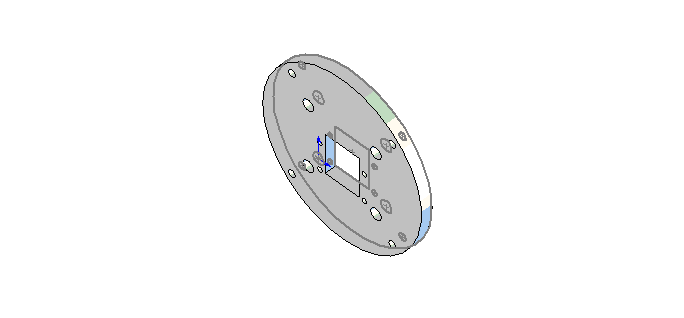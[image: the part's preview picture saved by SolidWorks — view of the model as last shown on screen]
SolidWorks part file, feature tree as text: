
SOLIDWORKS PART (.sldprt)
format: sldprt  version: not decoded by parser v0  size: 305,664 bytes
history: native  units: mm
features: sketch x4, plane x3, extrude x1 + 1 further entry (+7 scaffold rows collapsed)
feature tree (16):
  scaffold x7  (default folders/planes/origin — collapsed)
  "Corps de surface"
  plane  "Face"
  plane  "Dessus"
  plane  "Droite"
  sketch  "Esquisse1"  dims[c1.D1=4.8mm c1.D2=4.8mm c1.D7=4.8mm c1.D8=4.8mm c1.D17=~42.860884mm c1.D18=~42.860884mm c1.D3=32.0mm c1.D4=4.8mm c1.D5=8.0mm c1.D6=8.0mm c2.D7=4.8mm c2.D4=4.0mm c2.D5=5.6mm c2.D6=48.0mm c2.D9=32.0mm c2.D10=4.0mm c2.D11=5.6mm c2.D12=48.0mm c2.D13=28.8mm c2.D14=8.0mm c2.D15=8.0mm c2.D16=16.0mm c2.D18=48.0mm c3.D16=16.0mm c3.D17=8.0mm c3.D18=8.0mm c3.D19=4.0mm c3.D20=4.0mm c3.D21=24.0mm c3.D22=25.0mm c3.D13=28.8mm c3.D3=64.0mm c3.D12=8.0mm c4.D17=8.0mm c4.D9=8.0mm c4.D12=64.0mm c5.D17=48.0mm c5.D18=8.0mm c5.D9=32.0mm c6.D17=16.0mm c6.D18=16.0mm]
  sketch  "Esquisse5"  dims[c1.D12=2.1mm c1.D16=2.1mm c1.D1=8.0mm c1.D2=8.0mm c1.D3=4.0mm c1.D4=4.0mm c1.D5=25.0mm c1.D6=24.0mm c1.D7=12.5mm c1.D8=9.6mm c1.D9=5.5mm c1.D10=20.8mm c1.D11=10.4mm c1.D13=9.5mm c1.D14=2.0mm c1.D15=12.5mm c2.D16=~5.972653mm]
  sketch  "Esquisse7"  dims[c1.D1=75.0mm c1.D2=60.0mm c1.D3=3.1mm c1.D4=33.5mm c1.D5=33.5mm c2.D5=45.0deg c2.D6=~23.688077mm]
  sketch  "Esquisse6"  dims[D1=75.0mm D5=5.0mm D6=5.0mm D7=5.0mm D8=5.0mm D9=2.1mm D10=2.1mm D11=2.1mm D12=2.1mm D13=3.1mm D14=3.1mm D15=3.1mm D16=3.1mm D2=2.5mm D3=2.5mm D4=2.0mm]
  extrude  "Extrusion3"  Depth=5mm
decode coverage: 5 of 5 modeling features carry decoded parameters; 1 rows unclassified (native names shown)
note: ~ marks probable driven/reference dimensions
note: suppression state not decoded; provenance and decode notes live in map.json
